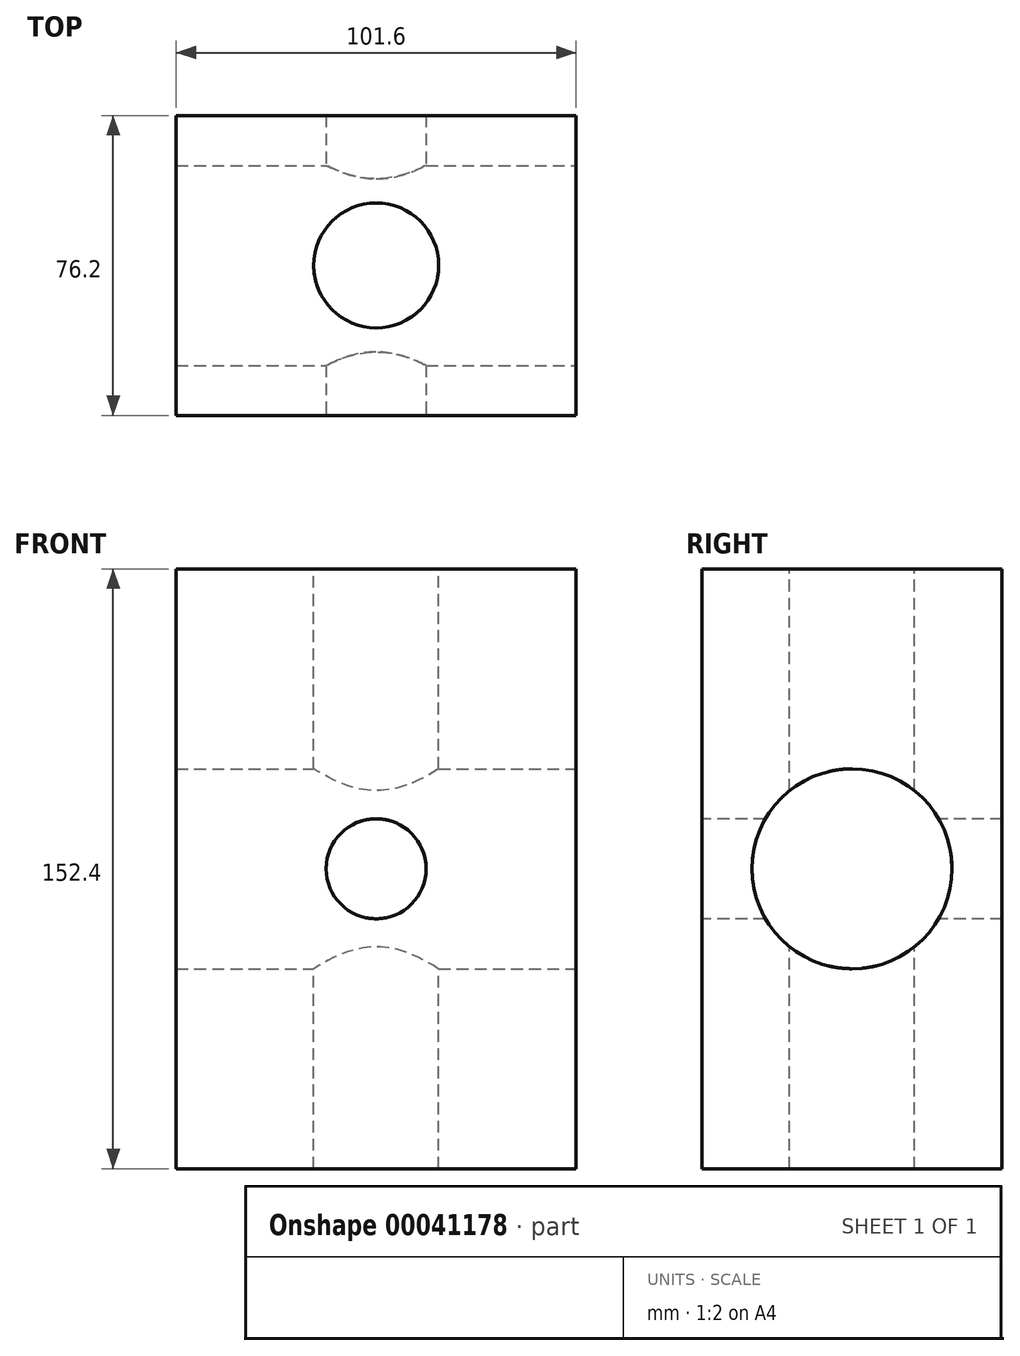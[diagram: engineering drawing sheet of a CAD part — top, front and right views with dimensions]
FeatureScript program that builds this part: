
annotation { "Feature Type Name" : "Feature", "Feature Type Description" : "" }
export const myFeature = defineFeature(function(context is Context, id is Id, definition is map)
    precondition{}
    {
        {
            var Q0;
            Q0=qCreatedBy(makeId("Front.planeOp"),FACE);
            var sketch = newSketch(context, id + "F0", { "sketchPlane" : qUnion([Q0])});
            skLineSegment(sketch, "E0.rect.bottom", {"start": v(50.8, 76.2) * mm, "end": v(-50.8, 76.2) * mm});
            skLineSegment(sketch, "E0.rect.top", {"start": v(50.8, -76.2) * mm, "end": v(-50.8, -76.2) * mm});
            skLineSegment(sketch, "E0.rect.left", {"start": v(50.8, 76.2) * mm, "end": v(50.8, -76.2) * mm});
            skLineSegment(sketch, "E0.rect.right", {"start": v(-50.8, 76.2) * mm, "end": v(-50.8, -76.2) * mm});
            skPoint(sketch, "E0.rect.middle", {"position": v(0, 0) * mm});
            skSolve(sketch);
        }
        {
            var Q0;
            Q0 = qSketchRegion(id + "F0", true);
            extrude(context, id + "F1", {"entities" : qUnion([Q0]), "endBound" : BoundingType.SYMMETRIC, "depth" : 76.2 * mm});
        }
        {
            var Q0;
            Q0=makeQuery(id+"F1.opExtrude","CAP_FACE",FACE,{"disambiguationData":[OSD([sQuery(id+"F0.wireOp",EDGE,"E0.rect.bottom"),sQuery(id+"F0.wireOp",EDGE,"E0.rect.top"),sQuery(id+"F0.wireOp",EDGE,"E0.rect.left"),sQuery(id+"F0.wireOp",EDGE,"E0.rect.right")])],"isStart":false});
            var sketch = newSketch(context, id + "F2", { "sketchPlane" : qUnion([Q0])});
            skCircle(sketch, "E1", {"center": v(0, 0) * mm, "radius": 12.7 * mm});
            skSolve(sketch);
        }
        {
            var Q0;
            Q0 = qSketchRegion(id + "F2", true);
            extrude(context, id + "F3", {"entities" : qUnion([Q0]), "operationType" : NewBodyOperationType.REMOVE, "endBound" : BoundingType.THROUGH_ALL, "oppositeDirection" : true, "depth" : 25.4 * mm});
        }
        {
            var Q0;
            Q0=makeQuery(id+"F1.opExtrude","SWEPT_FACE",FACE,{"disambiguationData":[OSD([sQuery(id+"F0.wireOp",EDGE,"E0.rect.left")])]});
            var sketch = newSketch(context, id + "F4", { "sketchPlane" : qUnion([Q0])});
            skCircle(sketch, "E2", {"center": v(0, 0) * mm, "radius": 25.4 * mm});
            skSolve(sketch);
        }
        {
            var Q0;
            Q0 = qSketchRegion(id + "F4", true);
            extrude(context, id + "F5", {"entities" : qUnion([Q0]), "operationType" : NewBodyOperationType.REMOVE, "endBound" : BoundingType.THROUGH_ALL, "oppositeDirection" : true, "depth" : 25.4 * mm});
        }
        {
            var Q0;
            Q0=makeQuery(id+"F1.opExtrude","SWEPT_FACE",FACE,{"disambiguationData":[OSD([sQuery(id+"F0.wireOp",EDGE,"E0.rect.bottom")])]});
            var sketch = newSketch(context, id + "F6", { "sketchPlane" : qUnion([Q0])});
            skCircle(sketch, "E3", {"center": v(0, 0) * mm, "radius": 15.88 * mm});
            skSolve(sketch);
        }
        {
            var Q0;
            Q0 = qSketchRegion(id + "F6", true);
            extrude(context, id + "F7", {"entities" : qUnion([Q0]), "operationType" : NewBodyOperationType.REMOVE, "endBound" : BoundingType.THROUGH_ALL, "oppositeDirection" : true, "depth" : 25.4 * mm});
        }
    });
